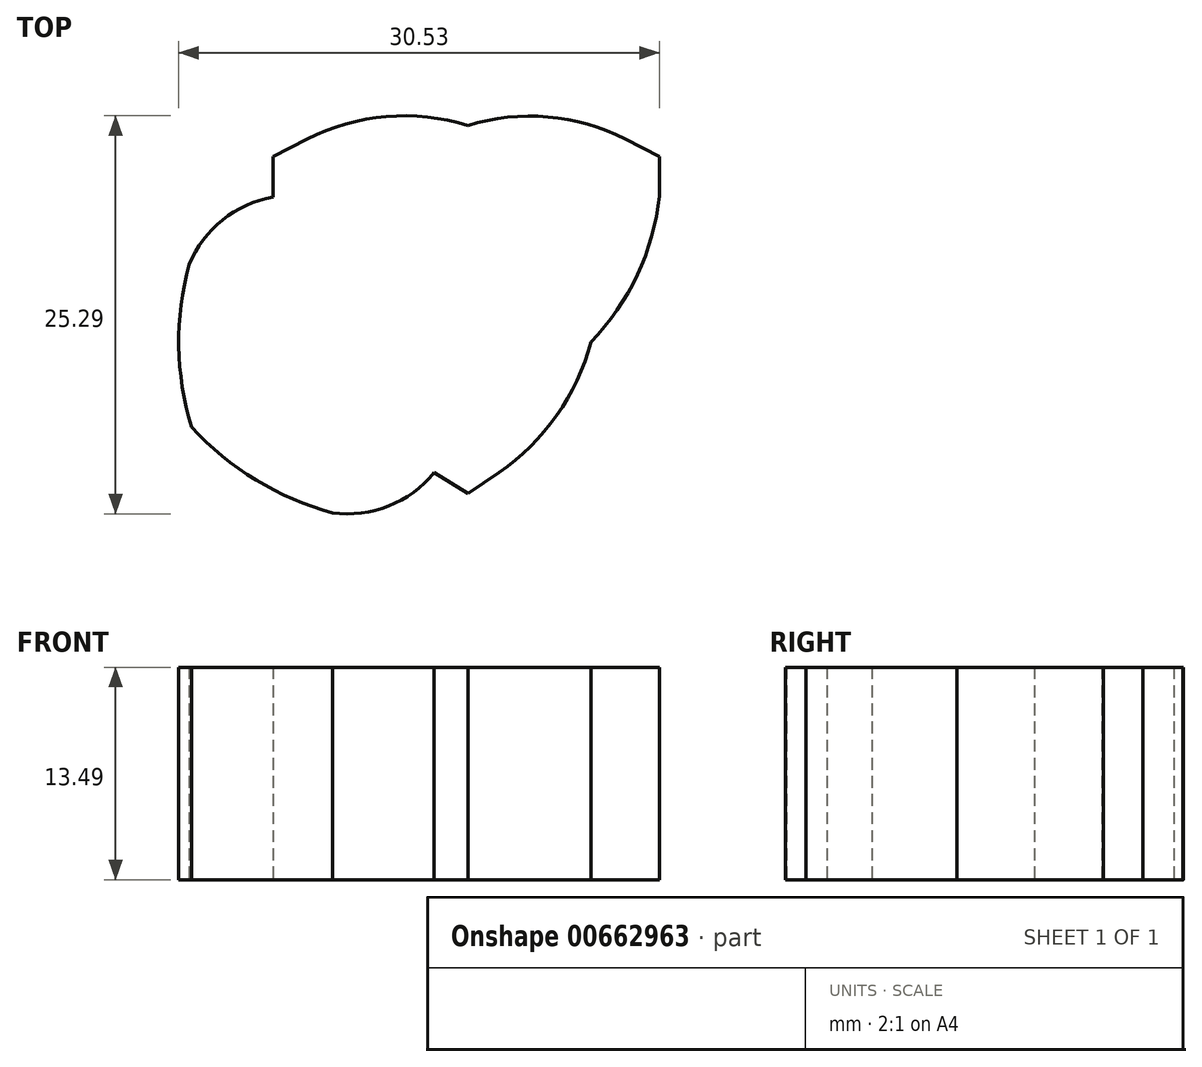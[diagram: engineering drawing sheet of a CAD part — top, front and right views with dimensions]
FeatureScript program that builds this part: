
annotation { "Feature Type Name" : "Feature", "Feature Type Description" : "" }
export const myFeature = defineFeature(function(context is Context, id is Id, definition is map)
    precondition{}
    {
        {
            var Q0;
            Q0=qCreatedBy(makeId("Top.planeOp"),FACE);
            var sketch = newSketch(context, id + "F0", { "sketchPlane" : qUnion([Q0])});
            skPoint(sketch, "E0.center", {"position": v(0, 0) * mm});
            skLineSegment(sketch, "E1", {"start": v(-10.2, 8.25) * mm, "end": v(-12.37, 7.15) * mm});
            skLineSegment(sketch, "E2", {"start": v(-12.37, 7.15) * mm, "end": v(-12.37, 4.64) * mm});
            skLineSegment(sketch, "E3.MirrorCS", {"start": v(12.16, 7.15) * mm, "end": v(12.16, 4.64) * mm});
            skLineSegment(sketch, "E4.MirrorCS", {"start": v(10, 8.25) * mm, "end": v(12.16, 7.15) * mm});
            skLineSegment(sketch, "E5", {"start": v(1.97, -12.9) * mm, "end": v(0, -14.26) * mm});
            skLineSegment(sketch, "E6", {"start": v(0, -14.26) * mm, "end": v(-2.14, -12.9) * mm});
            skArc(sketch, "E7", {"start": v(-8.6, -15.48) * mm, "mid": v(-5.03, -15.05) * mm, "end": v(-2.14, -12.9) * mm});
            skArc(sketch, "E8.MirrorCS", {"start": v(-17.7, 0.28) * mm, "mid": v(-15.6, 3.12) * mm, "end": v(-12.37, 4.57) * mm});
            skLineSegment(sketch, "E9", {"start": v(-12.37, 4.64) * mm, "end": v(-12.37, 4.57) * mm});
            skArc(sketch, "E10", {"start": v(-17.7, 0.28) * mm, "mid": v(-18.36, -4.89) * mm, "end": v(-17.55, -10.04) * mm});
            skArc(sketch, "E11", {"start": v(-17.55, -10.04) * mm, "mid": v(-13.46, -13.4) * mm, "end": v(-8.6, -15.48) * mm});
            skArc(sketch, "E12", {"start": v(0, 9.12) * mm, "mid": v(-5.19, 9.69) * mm, "end": v(-10.2, 8.25) * mm});
            skArc(sketch, "E13", {"start": v(10, 8.25) * mm, "mid": v(5.08, 9.66) * mm, "end": v(0, 9.12) * mm});
            skArc(sketch, "E14", {"start": v(1.97, -12.9) * mm, "mid": v(5.64, -9.3) * mm, "end": v(7.82, -4.64) * mm});
            skArc(sketch, "E15", {"start": v(7.82, -4.64) * mm, "mid": v(10.76, -0.36) * mm, "end": v(12.16, 4.64) * mm});
            skSolve(sketch);
        }
        {
            var Q0;
            Q0=makeQuery(id+"F0.imprint","IMPRINT",FACE,{"disambiguationData":[TD([[makeQuery(id+"F0.imprint","IMPRINT",EDGE,{"derivedFrom":sQuery(id+"F0.wireOp",EDGE,"E1")}),1.0]])]});
            extrude(context, id + "F1", {"entities" : qUnion([Q0]), "depth" : 13.5 * mm, "offsetDistance" : 25.4 * mm});
        }
    });
